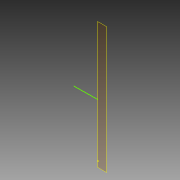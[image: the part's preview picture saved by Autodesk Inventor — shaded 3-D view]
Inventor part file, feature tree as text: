
AUTODESK INVENTOR PART (.ipt)
format: ipt  version: 2013 (Build 170138000, 138)  size: 55,296 bytes
history: native  units: in
note: dims shown in document units (in); Inventor stores cm internally (conversion verified against a paired STEP export)
features: plane x1, sketch x1
ambient origin geometry x8: Origin, YZ Plane, XZ Plane, XY Plane, X Axis, Y Axis, Z Axis, Center Point
feature tree (2):
  plane  "Work Plane1"
  sketch  "Sketch1"
